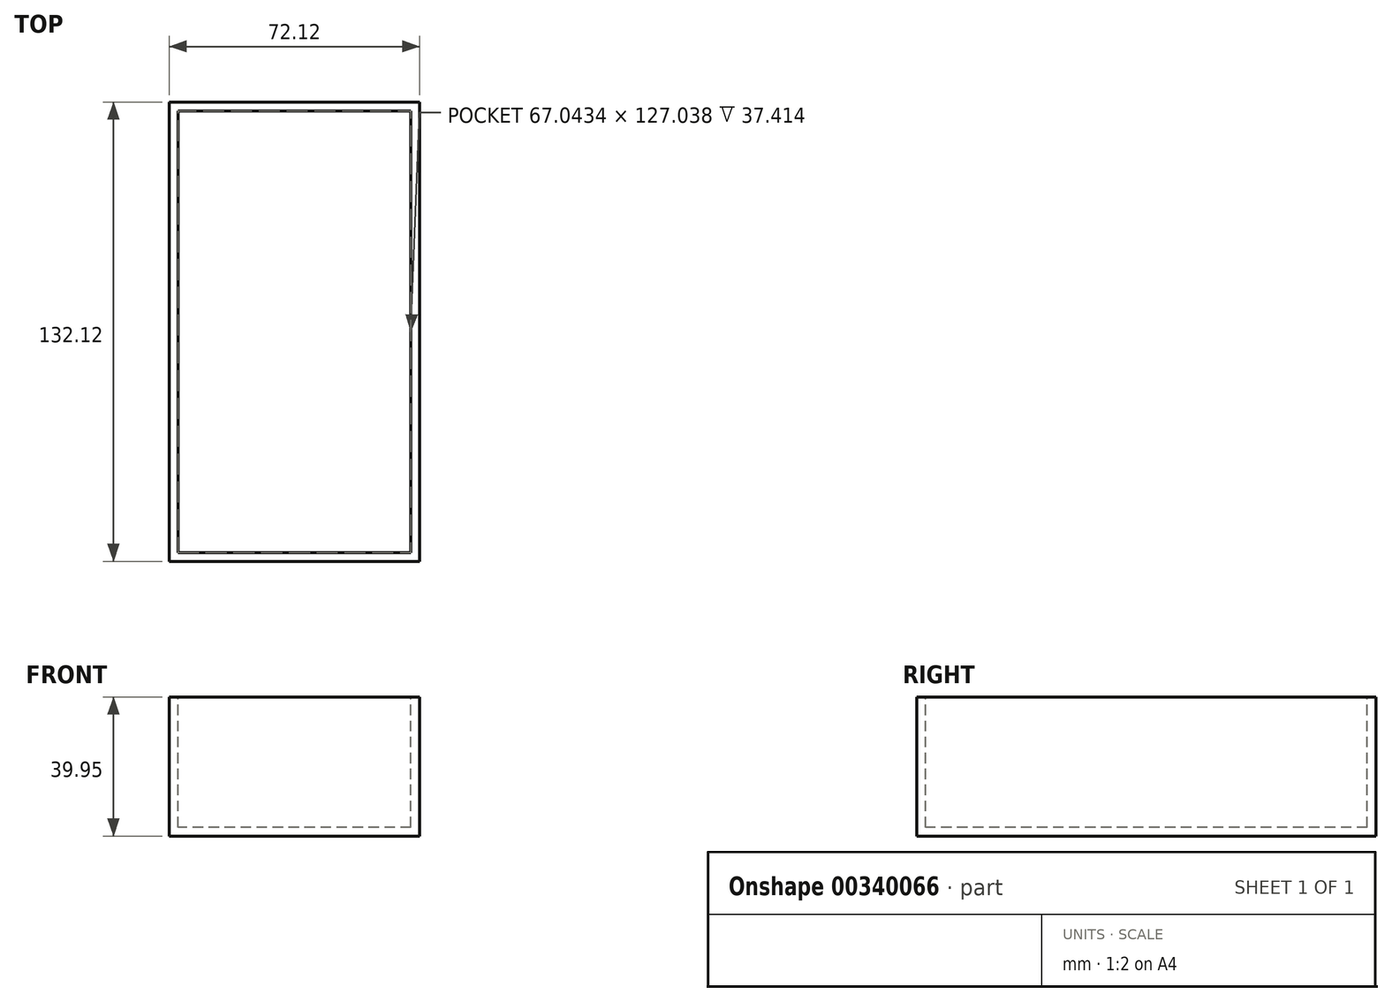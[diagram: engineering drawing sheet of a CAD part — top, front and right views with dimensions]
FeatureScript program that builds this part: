
annotation { "Feature Type Name" : "Feature", "Feature Type Description" : "" }
export const myFeature = defineFeature(function(context is Context, id is Id, definition is map)
    precondition{}
    {
        {
            var Q0;
            Q0=qCreatedBy(makeId("Top.planeOp"),FACE);
            var sketch = newSketch(context, id + "F0", { "sketchPlane" : qUnion([Q0])});
            skLineSegment(sketch, "E0.bottom", {"start": v(55.06, 66.06) * mm, "end": v(-55.06, 66.06) * mm});
            skLineSegment(sketch, "E0.top", {"start": v(55.06, -66.06) * mm, "end": v(-55.06, -66.06) * mm});
            skLineSegment(sketch, "E0.left", {"start": v(55.06, 66.06) * mm, "end": v(55.06, -66.06) * mm});
            skLineSegment(sketch, "E0.right", {"start": v(-55.06, 66.06) * mm, "end": v(-55.06, -66.06) * mm});
            skPoint(sketch, "E0.middle", {"position": v(0, 0) * mm});
            skSolve(sketch);
        }
        {
            var Q0;
            Q0 = qSketchRegion(id + "F0", true);
            extrude(context, id + "F1", {"entities" : qUnion([Q0]), "depth" : 39.95 * mm});
        }
        {
            var Q0;
            Q0=makeQuery(id+"F1.opExtrude","SWEPT_FACE",FACE,{"disambiguationData":[OSD([sQuery(id+"F0.wireOp",EDGE,"E0.right")])]});
            var sketch = newSketch(context, id + "F2", { "sketchPlane" : qUnion([Q0])});
            skLineSegment(sketch, "E1.bottom", {"start": v(66.06, 0) * mm, "end": v(-66.06, 0) * mm});
            skLineSegment(sketch, "E1.top", {"start": v(66.06, 38.68) * mm, "end": v(-66.06, 38.68) * mm});
            skLineSegment(sketch, "E1.left", {"start": v(66.06, 0) * mm, "end": v(66.06, 38.68) * mm});
            skLineSegment(sketch, "E1.right", {"start": v(-66.06, 0) * mm, "end": v(-66.06, 38.68) * mm});
            skSolve(sketch);
        }
        {
            var Q0;
            Q0 = qSketchRegion(id + "F2", true);
            extrude(context, id + "F3", {"entities" : qUnion([Q0]), "operationType" : NewBodyOperationType.REMOVE, "oppositeDirection" : true, "depth" : 19 * mm});
        }
        {
            var Q0;
            Q0=makeQuery(id+"F1.opExtrude","SWEPT_FACE",FACE,{"disambiguationData":[OSD([sQuery(id+"F0.wireOp",EDGE,"E0.left")])]});
            var sketch = newSketch(context, id + "F4", { "sketchPlane" : qUnion([Q0])});
            skLineSegment(sketch, "E2.bottom", {"start": v(-66.06, 0) * mm, "end": v(66.06, 0) * mm});
            skLineSegment(sketch, "E2.top", {"start": v(-66.06, 38.68) * mm, "end": v(66.06, 38.68) * mm});
            skLineSegment(sketch, "E2.left", {"start": v(-66.06, 0) * mm, "end": v(-66.06, 38.68) * mm});
            skLineSegment(sketch, "E2.right", {"start": v(66.06, 0) * mm, "end": v(66.06, 38.68) * mm});
            skSolve(sketch);
        }
        {
            var Q0;
            Q0 = qSketchRegion(id + "F4", true);
            extrude(context, id + "F5", {"entities" : qUnion([Q0]), "operationType" : NewBodyOperationType.REMOVE, "oppositeDirection" : true, "depth" : 19 * mm});
        }
        {
            var Q0;
            Q0=makeQuery(id+"F3.boolean.opBoolean","COPY",FACE,{"derivedFrom":makeQuery(id+"F3.opExtrude","SWEPT_FACE",FACE,{"disambiguationData":[OSD([sQuery(id+"F2.wireOp",EDGE,"E1.top")])]})});
            var sketch = newSketch(context, id + "F6", { "sketchPlane" : qUnion([Q0])});
            skLineSegment(sketch, "E3.bottom", {"start": v(-55.06, -66.06) * mm, "end": v(-36.06, -66.06) * mm});
            skLineSegment(sketch, "E3.top", {"start": v(-55.06, 66.06) * mm, "end": v(-36.06, 66.06) * mm});
            skLineSegment(sketch, "E3.left", {"start": v(-55.06, -66.06) * mm, "end": v(-55.06, 66.06) * mm});
            skLineSegment(sketch, "E3.right", {"start": v(-36.06, -66.06) * mm, "end": v(-36.06, 66.06) * mm});
            skSolve(sketch);
        }
        {
            var Q0;
            Q0 = qSketchRegion(id + "F6", true);
            extrude(context, id + "F7", {"entities" : qUnion([Q0]), "operationType" : NewBodyOperationType.REMOVE, "endBound" : BoundingType.THROUGH_ALL, "oppositeDirection" : true, "depth" : 25.4 * mm});
        }
        {
            var Q0;
            Q0=makeQuery(id+"F5.boolean.opBoolean","COPY",FACE,{"derivedFrom":makeQuery(id+"F5.opExtrude","SWEPT_FACE",FACE,{"disambiguationData":[OSD([sQuery(id+"F4.wireOp",EDGE,"E2.top")])]})});
            var sketch = newSketch(context, id + "F8", { "sketchPlane" : qUnion([Q0])});
            skLineSegment(sketch, "E4.bottom", {"start": v(36.06, 66.06) * mm, "end": v(55.06, 66.06) * mm});
            skLineSegment(sketch, "E4.top", {"start": v(36.06, -66.06) * mm, "end": v(55.06, -66.06) * mm});
            skLineSegment(sketch, "E4.left", {"start": v(36.06, 66.06) * mm, "end": v(36.06, -66.06) * mm});
            skLineSegment(sketch, "E4.right", {"start": v(55.06, 66.06) * mm, "end": v(55.06, -66.06) * mm});
            skSolve(sketch);
        }
        {
            var Q0;
            Q0 = qSketchRegion(id + "F8", true);
            extrude(context, id + "F9", {"entities" : qUnion([Q0]), "operationType" : NewBodyOperationType.REMOVE, "endBound" : BoundingType.THROUGH_ALL, "oppositeDirection" : true, "depth" : 25.4 * mm});
        }
        {
            var Q0;
            Q0=makeQuery(id+"F1.opExtrude","CAP_FACE",FACE,{"disambiguationData":[OSD([sQuery(id+"F0.wireOp",EDGE,"E0.bottom"),sQuery(id+"F0.wireOp",EDGE,"E0.top"),sQuery(id+"F0.wireOp",EDGE,"E0.left"),sQuery(id+"F0.wireOp",EDGE,"E0.right")])],"isStart":false});
            var sketch = newSketch(context, id + "F10", { "sketchPlane" : qUnion([Q0])});
            skLineSegment(sketch, "E5.bottom", {"start": v(33.52, 63.52) * mm, "end": v(-33.52, 63.52) * mm});
            skLineSegment(sketch, "E5.top", {"start": v(33.52, -63.52) * mm, "end": v(-33.52, -63.52) * mm});
            skLineSegment(sketch, "E5.left", {"start": v(33.52, 63.52) * mm, "end": v(33.52, -63.52) * mm});
            skLineSegment(sketch, "E5.right", {"start": v(-33.52, 63.52) * mm, "end": v(-33.52, -63.52) * mm});
            skPoint(sketch, "E5.middle", {"position": v(0, 0) * mm});
            skSolve(sketch);
        }
        {
            var Q0;
            Q0 = qSketchRegion(id + "F10", true);
            extrude(context, id + "F11", {"entities" : qUnion([Q0]), "operationType" : NewBodyOperationType.REMOVE, "oppositeDirection" : true, "depth" : 37.4 * mm});
        }
    });
